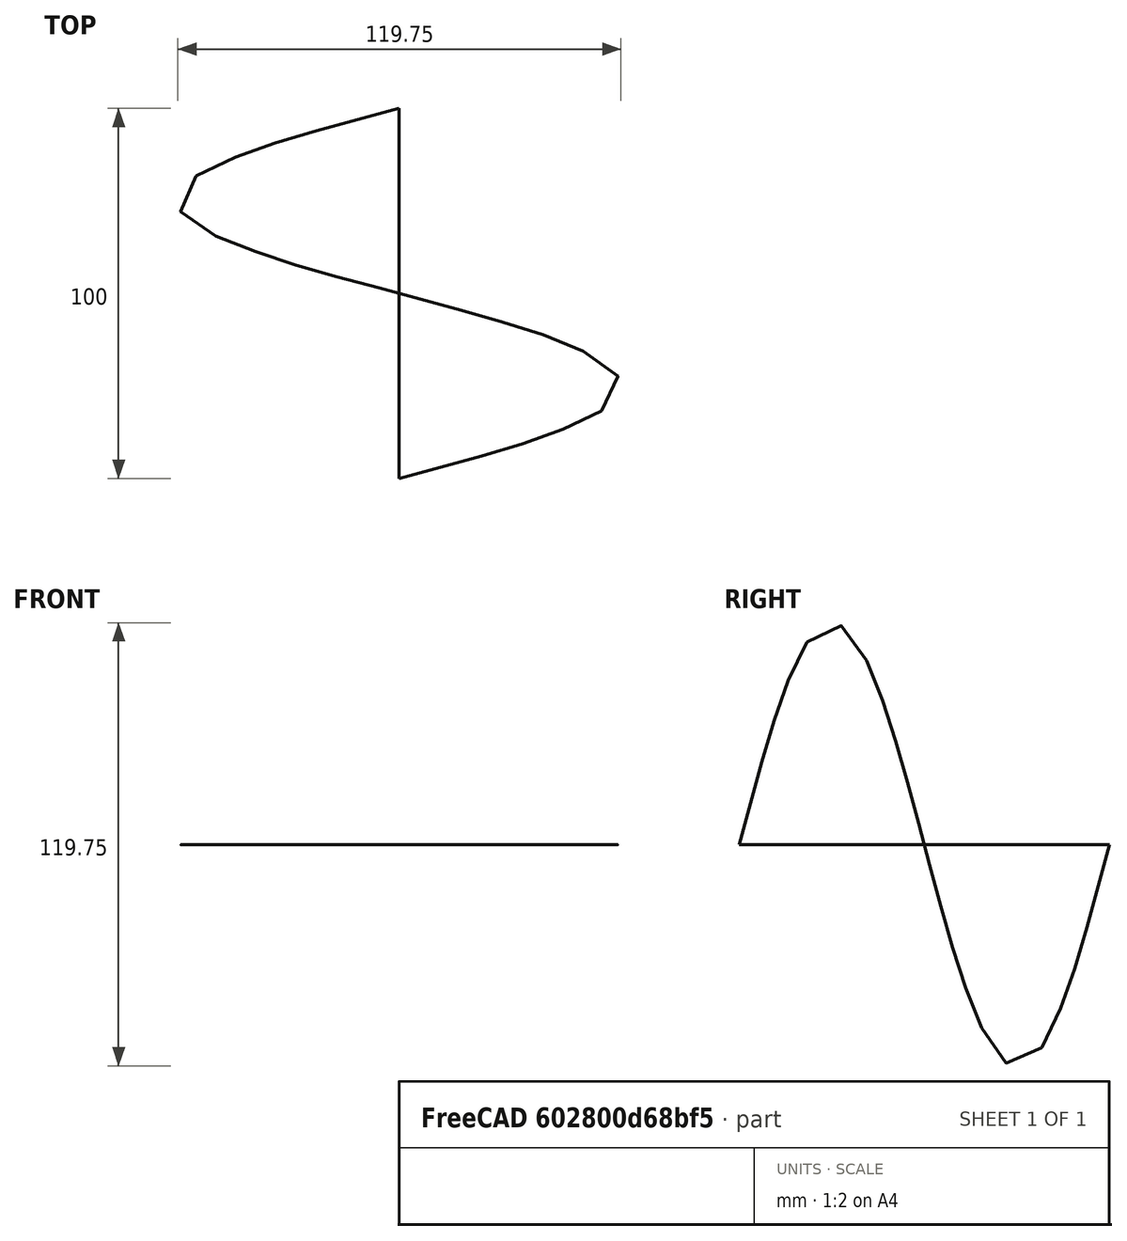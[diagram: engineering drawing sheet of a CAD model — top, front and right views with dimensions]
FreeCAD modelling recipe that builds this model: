
FCSTD DOCUMENT  (FreeCAD 0.20R24693 (Git))
Label: MAGNETIC ELECTRIC WAVE
License: All rights reserved
LicenseURL: http://en.wikipedia.org/wiki/All_rights_reserved
objects: PartDesign::CoordinateSystem×5, Part::Line×3, App::Part×3, App::DocumentObjectGroup×2, App::Link×2, App::FeaturePython×1, Part::Part2DObjectPython×1, Part::RuledSurface×1, Part::Feature×1, Part::Compound×1, Part::FeaturePython×1
note: 12 computed .brp shape members not serialized (recipe doc carries the construction recipe); baked Part::Feature solids carry a one-line shape summary decoded from their .brp

FEATURE [Part::Line] Line
  AttacherType = Attacher::AttachEngine3D
  Placement = pos=(0,58,0) rot=(0,0,1;0rad)
  X1 = 0
  X2 = -28.9052
  Y1 = 0
  Y2 = 0
  Z1 = 0
  Z2 = 0
  expr: X2 = sin(Variables.time * 3.6) * 60
  expr: .Placement.Base.y = Variables.time
FEATURE [Part::Line] Line001
  AttacherType = Attacher::AttachEngine3D
  Placement = pos=(0,58,0) rot=(0,0,1;0rad)
  X1 = 0
  X2 = 0
  Y1 = 0
  Y2 = 0
  Z1 = 0
  Z2 = -28.9052
  expr: Z2 = sin(Variables.time * 3.6) * 60
  expr: .Placement.Base.y = Variables.time
FEATURE [Part::Line] Line002
  AttacherType = Attacher::AttachEngine3D
  X1 = 0
  X2 = 0
  Y1 = 0
  Y2 = 100
  Z1 = 0
  Z2 = 0
FEATURE [PartDesign::CoordinateSystem] LCS_Origin
  AttacherType = Attacher::AttachEngine3D
  MapMode = 2
  Support = -> [X_Axis]
FEATURE [App::DocumentObjectGroup] Constraints
FEATURE [App::FeaturePython] Variables  # WARN: FeaturePython — macro-defined, semantics opaque (R4)
  time = 58
FEATURE [PartDesign::CoordinateSystem] LCS_0
  AttacherType = Attacher::AttachEngine3D
  MapMode = 2
  Support = -> [X_Axis001]
FEATURE [PartDesign::CoordinateSystem] LCS_0001
  AttacherType = Attacher::AttachEngine3D
  MapMode = 2
  Support = -> [X_Axis002]
FEATURE [PartDesign::CoordinateSystem] LCS_1
  AttacherType = Attacher::AttachEngine3D
FEATURE [App::Part] Part
  Group = -> [LCS_0,Line,LCS_1]
  Origin = -> Origin001
FEATURE [PartDesign::CoordinateSystem] LCS_2
  AttacherType = Attacher::AttachEngine3D
FEATURE [App::Part] Part_2
  Group = -> [LCS_0001,Line001,LCS_2]
  Origin = -> Origin002
FEATURE [App::DocumentObjectGroup] Parts
  Group = -> [Part,Part_2]
FEATURE [App::Link] Part001
  AssemblyType = Asm4EE
  AttachedBy = #LCS_1
  AttachedTo = Parent Assembly#LCS_Origin
  LinkedObject = -> Part
  expr: Placement = LCS_Origin.Placement * AttachmentOffset * LCS_1.Placement ^ -1
FEATURE [App::Link] Part_2001
  AssemblyType = Asm4EE
  AttachedBy = #LCS_2
  AttachedTo = Parent Assembly#LCS_Origin
  LinkedObject = -> Part_2
  expr: Placement = LCS_Origin.Placement * AttachmentOffset * LCS_2.Placement ^ -1
FEATURE [App::Part] Model
  Configuration = 0
  Group = -> [LCS_Origin,Constraints,Variables,Part001,Part_2001]
  Origin = -> Origin
  Type = Assembly4 Model
FEATURE [Part::Part2DObjectPython] BSpline  # Draft 2D object (typed FeaturePython)
  Area = 0
  Closed = false
  MakeFace = true
  Parameterization = 1
  Points = (26) [(0,0,0),(7.51999,2,0),(11.2429,3,0),(18.541,5,0),(28.9052,8,0),(35.2671,10,0),(41.0728,12,0),(48.541,15,0),(54.2896,18,0),(58.9372,22,0),(60,25,0),+15 more]
FEATURE [Part::RuledSurface] Ruled_Surface
  Curve1 = -> BSpline
  Curve2 = -> Line002
  Orientation = 0
FEATURE [Part::Feature] Ruled_Surface001
  Placement = pos=(0,0,0) rot=(0,1,0;4.71239rad)
  shape: bbox 2e-07 x 100 x 121.2 mm, 1 faces, 0 solids (baked)
FEATURE [Part::Compound] Compound
  Links = -> [Ruled_Surface,Ruled_Surface001]
FEATURE [Part::FeaturePython] Array  # Draft array (typed FeaturePython)
  Angle = 360
  ArrayType = 0
  Axis = (0,0,1)
  Base = -> Compound
  Center = (0,0,0)
  Count = 4
  ExpandArray = false
  Fuse = false
  IntervalAxis = (0,0,0)
  IntervalX = (0,100,0)
  IntervalY = (0,100,0)
  IntervalZ = (0,0,100)
  NumberCircles = 3
  NumberPolar = 5
  NumberX = 1
  NumberY = 4
  NumberZ = 1
  PlacementList = 4 placements: arithmetic series from (0,0,0) step (0,100,0) to (0,300,0)
  RadialDistance = 50
  ScaleList = (4) [(1,1,1),(1,1,1),(1,1,1),(1,1,1)]
  Symmetry = 1
  TangentialDistance = 25
